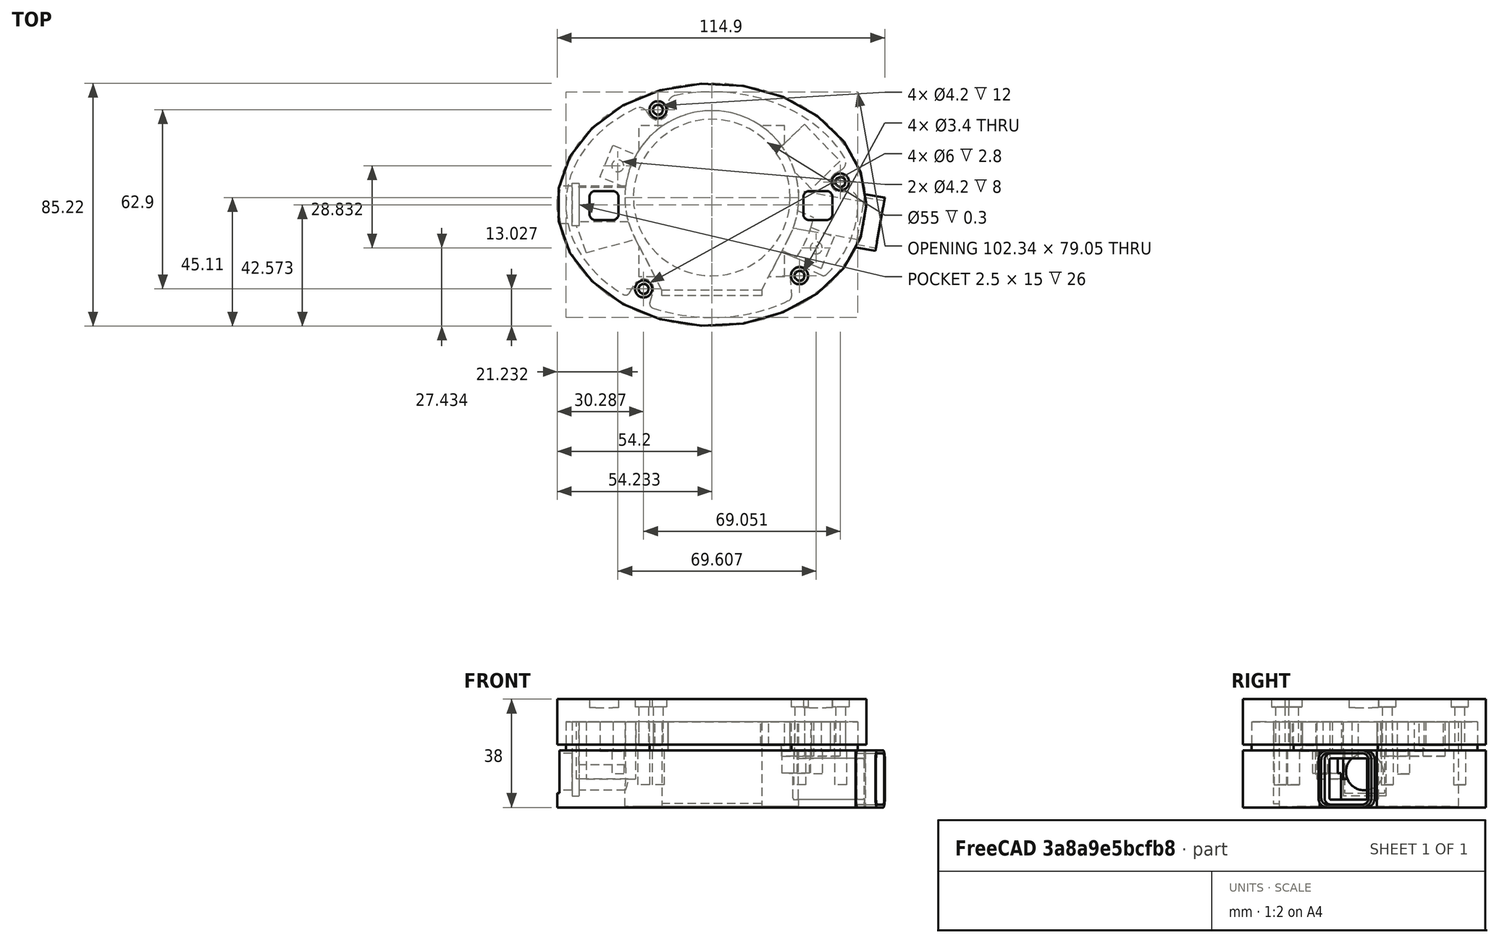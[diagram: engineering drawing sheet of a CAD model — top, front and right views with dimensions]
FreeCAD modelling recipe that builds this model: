
FCSTD DOCUMENT  (FreeCAD 0.21R32637 (Git))
Label: RGB-Case-Ellipse-SmallModel
License: All rights reserved
LicenseURL: http://en.wikipedia.org/wiki/All_rights_reserved
objects: Sketcher::SketchObject×25, PartDesign::Pocket×16, PartDesign::Line×8, PartDesign::Pad×5, PartDesign::Hole×5, PartDesign::Plane×2, PartDesign::SubShapeBinder×2, PartDesign::Body×2, PartDesign::SubtractiveCylinder×1, PartDesign::SubtractiveBox×1, PartDesign::ShapeBinder×1, PartDesign::FeatureBase×1
note: 97 computed .brp shape members not serialized (recipe doc carries the construction recipe); baked Part::Feature solids carry a one-line shape summary decoded from their .brp

FEATURE [Sketcher::SketchObject] Sketch
  FullyConstrained = true
  MapMode = 5
  Support = -> [XY_Plane001]
  sketch-geometry (9):
    g0: Ellipse CenterX=0 CenterY=0 CenterZ=0 NormalX=0 NormalY=0 NormalZ=1 MajorRadius=54.2041 MinorRadius=42.6127 AngleXU=-3.14159
    g1: LineSegment StartX=-54.2041 StartY=0 StartZ=0 EndX=54.2041 EndY=0 EndZ=0
    g2: LineSegment StartX=-1.358e-13 StartY=-42.6127 StartZ=0 EndX=1.358e-13 EndY=42.6127 EndZ=0
    g3: GeomPoint X=-33.5 Y=-1.727e-13 Z=0
    g4: GeomPoint X=33.5 Y=1.727e-13 Z=0
    g5: LineSegment StartX=-33.5 StartY=33.5 StartZ=0 EndX=33.5 EndY=33.5 EndZ=0
    g6: LineSegment StartX=33.5 StartY=33.5 StartZ=0 EndX=33.5 EndY=-33.5 EndZ=0
    g7: LineSegment StartX=33.5 StartY=-33.5 StartZ=0 EndX=-33.5 EndY=-33.5 EndZ=0
    g8: LineSegment StartX=-33.5 StartY=-33.5 StartZ=0 EndX=-33.5 EndY=33.5 EndZ=0
  constraints (17):
    c: InternalAlignment(g1-g4 -> g0) x4
    c: Coincident(g0,g-1)
    c: Horizontal(g1)
    c: Coincident(g5,g6)
    c: Coincident(g6,g7)
    c: Coincident(g7,g8)
    c: Coincident(g8,g5)
    c: Horizontal(g5)
    c: Horizontal(g7)
    c: Vertical(g6)
    c: Vertical(g8)
    c: PointOnObject(g5,g0)
    c: Symmetric(g5,g6,g0)
    c: DistanceY(g6,g6) = 67
    c: Equal(g6,g7)
    c: PointOnObject(g4,g6)
    c: DistanceX(g1,g3) = 20.7041
FEATURE [PartDesign::Pad] Pad  label="Aussenform"
  Direction = (0,0,1)
  Length = 30
  Length2 = 10
  Profile = -> Sketch
  ReferenceAxis = -> Sketch [N_Axis]
  Refine = true
  Type = 0
FEATURE [Sketcher::SketchObject] Sketch001
  ExternalGeometry = -> [Pad]
  FullyConstrained = true
  MapMode = 5
  Placement = pos=(0,0,30) rot=(0,0,1;0rad)
  Support = -> [Pad]
  expr: Constraints[11] = 65 / 2
  sketch-geometry (6):
    g0: LineSegment StartX=17.5 StartY=-30 StartZ=0 EndX=-17.5 EndY=-30 EndZ=0
    g1: ArcOfCircle CenterX=0 CenterY=2.5 CenterZ=0 NormalX=0 NormalY=0 NormalZ=1 AngleXU=0 Radius=30.5 StartAngle=5.80464 EndAngle=9.90332
    g2: LineSegment StartX=-17.5 StartY=-30 StartZ=0 EndX=-27.0738 EndY=-11.5449 EndZ=0
    g3: LineSegment StartX=17.5 StartY=-30 StartZ=0 EndX=27.0738 EndY=-11.5449 EndZ=0
    g4: GeomPoint X=0 Y=-30 Z=0
    g5: Circle CenterX=0 CenterY=2.5 CenterZ=0 NormalX=0 NormalY=0 NormalZ=1 AngleXU=0 Radius=30.5
  constraints (14):
    c: Horizontal(g0)
    c: DistanceX(g0,g0) = 35
    c: Diameter(g1) = 61
    c: DistanceY(g-1,g1) = 2.5
    c: PointOnObject(g1,g-2)
    c: Coincident(g2,g0)
    c: Coincident(g3,g0)
    c: Tangent(g1,g3) = -1.5708
    c: Tangent(g1,g2) = 1.5708
    c: PointOnObject(g4,g-2)
    c: Symmetric(g0,g0,g4)
    c: DistanceY(g4,g1) = 32.5
    c: Coincident(g5,g1)
    c: Equal(g5,g1)
FEATURE [PartDesign::Pocket] Pocket  label="Ausschnitt T-RGB"
  BaseFeature = -> Pad
  Direction = (0,0,-1)
  Length = 29.7
  Length2 = 5
  Profile = -> Sketch001
  ReferenceAxis = -> Sketch001 [N_Axis]
  Refine = true
  Type = 0
  expr: Length = <<Aussenform>>.Length - 0.3 mm
FEATURE [PartDesign::SubtractiveCylinder] Cylinder  label="Fenster Display"
  Angle = 360
  AttacherType = Attacher::AttachEngine3D
  BaseFeature = -> Pocket
  FirstAngle = 0
  Height = 2
  MapMode = 11
  Placement = pos=(3.6e-15,2.5,0.3) rot=(-0.519381,0.854543,0;3.14159rad)
  Radius = 27.5
  Refine = true
  SecondAngle = 0
  Support = -> [Pocket]
FEATURE [PartDesign::Plane] DatumPlane  label="DatumPlane - Height T-RGB"
  AttachmentOffset = pos=(0,0,19.5) rot=(0,0,1;0rad)
  Length = 134.685
  MapMode = 45
  Placement = pos=(-2.63e-14,-4.82293,19.8) rot=(0,0,1;0rad)
  ResizeMode = 0
  Support = -> [Cylinder]
  Width = 104.953
FEATURE [PartDesign::SubtractiveBox] Box  label="Box - Akku"
  AttacherType = Attacher::AttachEngine3D
  AttachmentOffset = pos=(-25.5,-20.5,2) rot=(0,0,1;0rad)
  BaseFeature = -> Cylinder
  Height = 16
  Length = 51
  MapMode = 5
  Placement = pos=(-25.5,-25.3229,21.8) rot=(0,0,1;0rad)
  Refine = true
  Support = -> [DatumPlane]
  Width = 53
  expr: .AttachmentOffset.Base.x = -Length / 2
  expr: .AttachmentOffset.Base.y = -(Width / 2) + 6 mm
FEATURE [PartDesign::Plane] DatumPlane001  label="DatumPlane - Height Battery"
  AttachmentOffset = pos=(0,0,7.5) rot=(0,0,1;0rad)
  Length = 134.685
  MapMode = 5
  Placement = pos=(-25.5,-25.3229,29.3) rot=(0,0,1;0rad)
  ResizeMode = 0
  Support = -> [Box]
  Width = 104.953
FEATURE [Sketcher::SketchObject] Sketch002
  ExternalGeometry = -> [Pad]
  FullyConstrained = true
  MapMode = 5
  Placement = pos=(0,0,30) rot=(0,0,1;0rad)
  Support = -> [Pad]
  sketch-geometry (12):
    g0: Ellipse CenterX=0 CenterY=0 CenterZ=0 NormalX=0 NormalY=0 NormalZ=1 MajorRadius=51.2041 MinorRadius=39.6127 AngleXU=0
    g1: LineSegment StartX=51.2041 StartY=0 StartZ=0 EndX=-51.2041 EndY=0 EndZ=0
    g2: LineSegment StartX=0 StartY=39.6127 StartZ=0 EndX=0 EndY=-39.6127 EndZ=0
    g3: GeomPoint X=32.4454 Y=0 Z=0
    g4: GeomPoint X=-32.4454 Y=0 Z=0
    g5: GeomPoint X=0 Y=42.6127 Z=0
    g6: GeomPoint X=54.2041 Y=0 Z=0
    g7: Ellipse CenterX=0 CenterY=0 CenterZ=0 NormalX=0 NormalY=0 NormalZ=1 MajorRadius=54.2041 MinorRadius=42.6127 AngleXU=-3.14159
    g8: LineSegment StartX=-54.2041 StartY=0 StartZ=0 EndX=54.2041 EndY=0 EndZ=0
    g9: LineSegment StartX=0 StartY=-42.6127 StartZ=0 EndX=0 EndY=42.6127 EndZ=0
    g10: GeomPoint X=-33.5 Y=0 Z=0
    g11: GeomPoint X=33.5 Y=0 Z=0
  constraints (12):
    c: InternalAlignment(g1-g4 -> g0) x4
    c: Coincident(g0,g-3)
    c: PointOnObject(g1,g-1)
    c: PointOnObject(g5,g-3)
    c: PointOnObject(g6,g-3)
    c: PointOnObject(g6,g-1)
    c: DistanceY(g2,g5) = 3
    c: DistanceX(g1,g6) = 3
    c: InternalAlignment(g8-g11 -> g7) x4
    c: Coincident(g7,g0)
    c: Coincident(g8,g6)
    c: Coincident(g9,g5)
FEATURE [PartDesign::Pocket] Pocket001  label="Pocket - Counterpart"
  BaseFeature = -> Box
  Direction = (0,0,-1)
  Length = 10
  Length2 = 5
  Placement = pos=(-25.5,-25.3229,21.8) rot=(0,0,1;0rad)
  Profile = -> Sketch002
  ReferenceAxis = -> Sketch002 [N_Axis]
  Refine = true
  Type = 0
  expr: Length = <<Aussenform>>.Length - 20 mm
FEATURE [Sketcher::SketchObject] Sketch003  label="Sketch SD"
  ExternalGeometry = -> [Pocket]
  FullyConstrained = true
  MapMode = 5
  Placement = pos=(0,0,30) rot=(0,0,1;0rad)
  Support = -> [Pocket]
  sketch-geometry (8):
    g0: LineSegment StartX=29.8059 StartY=-18.2995 StartZ=0 EndX=-2.93048 EndY=-4.40379 EndZ=0
    g1: LineSegment StartX=-2.93048 StartY=-4.40379 StartZ=0 EndX=2.93048 EndY=9.40379 EndZ=0
    g2: LineSegment StartX=2.93048 StartY=9.40379 StartZ=0 EndX=35.6668 EndY=-4.49198 EndZ=0
    g3: LineSegment StartX=32.7364 StartY=-11.3958 StartZ=0 EndX=0 EndY=2.5 EndZ=0
    g4: GeomPoint X=35.6668 Y=-4.49198 Z=0
    g5: GeomPoint X=30.1438 Y=-2.14759 Z=0
    g6: LineSegment StartX=35.6668 StartY=-4.49198 StartZ=0 EndX=29.8059 EndY=-18.2995 EndZ=0
    g7: ArcOfCircle CenterX=0 CenterY=2.5 CenterZ=0 NormalX=0 NormalY=0 NormalZ=1 AngleXU=0 Radius=36.3457 StartAngle=5.67391 EndAngle=6.0896
  constraints (18):
    c: Coincident(g0,g1)
    c: Coincident(g1,g2)
    c: Parallel(g0,g2)
    c: Perpendicular(g1,g2)
    c: Coincident(g4,g2)
    c: Coincident(g3,g-3)
    c: Angle(g-1,g3) = 2.74017
    c: PointOnObject(g5,g-3)
    c: PointOnObject(g5,g2)
    c: Distance(g5,g2) = 6
    c: Coincident(g6,g2)
    c: Coincident(g0,g6)
    c: Symmetric(g0,g1,g3)
    c: Distance(g1) = 15
    c: Coincident(g7,g3)
    c: Coincident(g7,g2)
    c: Coincident(g7,g0)
    c: Symmetric(g0,g2,g3)
FEATURE [PartDesign::Pocket] Pocket002  label="Pocket - SD"
  BaseFeature = -> Pocket001
  Direction = (0,0,-1)
  Length = 18
  Length2 = 20
  Placement = pos=(-25.5,-25.3229,21.8) rot=(0,0,1;0rad)
  Profile = -> Sketch003
  ReferenceAxis = -> Sketch003 [N_Axis]
  Refine = true
  Type = 0
  expr: Length = <<Aussenform>>.Length - 12 mm
FEATURE [Sketcher::SketchObject] Sketch004  label="Sketch USB-C"
  ExternalGeometry = -> [Pocket,Pad]
  FullyConstrained = true
  MapMode = 5
  Placement = pos=(0,0,30) rot=(0,0,1;0rad)
  Support = -> [Pocket]
  sketch-geometry (18):
    g0: LineSegment StartX=-29.2703 StartY=2.16279 StartZ=0 EndX=-49.0332 EndY=-3.13265 EndZ=0
    g1: LineSegment StartX=-47.7751 StartY=-2.79554 StartZ=0 EndX=-44.0222 EndY=-16.8015 EndZ=0
    g2: LineSegment StartX=-44.0222 StartY=-16.8015 StartZ=0 EndX=-25.5175 EndY=-11.8431 EndZ=0
    g3: LineSegment StartX=-25.5175 StartY=-11.8431 StartZ=0 EndX=-30.2985 EndY=6 EndZ=0
    g4: LineSegment StartX=-46.5277 StartY=-9.96706 StartZ=0 EndX=0 EndY=2.5 EndZ=0
    g5: ArcOfEllipse CenterX=0 CenterY=0 CenterZ=0 NormalX=0 NormalY=0 NormalZ=1 MajorRadius=49.2041 MinorRadius=37.6127 AngleXU=3.14159 StartAngle=0.0833837 EndAngle=0.46307
    g6: LineSegment StartX=-49.2041 StartY=0 StartZ=0 EndX=49.2041 EndY=0 EndZ=0
    g7: LineSegment StartX=0 StartY=-37.6127 StartZ=0 EndX=0 EndY=37.6127 EndZ=0
    g8: GeomPoint X=-31.7228 Y=0 Z=0
    g9: GeomPoint X=31.7228 Y=0 Z=0
    g10: GeomPoint X=0 Y=42.6127 Z=0
    g11: LineSegment StartX=0 StartY=37.6127 StartZ=0 EndX=0 EndY=42.6127 EndZ=0
    g12: LineSegment StartX=-49.2041 StartY=0 StartZ=0 EndX=-54.2041 EndY=0 EndZ=0
    g13: LineSegment StartX=-44.0222 StartY=-16.8015 StartZ=0 EndX=-49.0332 EndY=-3.13265 EndZ=0
    g14: LineSegment StartX=-30.2985 StartY=6 StartZ=0 EndX=-49.0332 EndY=6 EndZ=0
    g15: LineSegment StartX=-49.0332 StartY=-3.13265 StartZ=0 EndX=-49.0332 EndY=6 EndZ=0
    g16: GeomPoint X=-27.3939 Y=-4.84017 Z=0
    g17: GeomPoint X=-27.3939 Y=-4.84017 Z=0
  constraints (38):
    c: Coincident(g1,g2)
    c: Coincident(g2,g3)
    c: Parallel(g3,g1)
    c: Perpendicular(g3,g2)
    c: Perpendicular(g4,g1)
    c: Symmetric(g1,g0,g4)
    c: Angle(g-2,g4) = 1.8326
    c: Parallel(g0,g2)
    c: InternalAlignment(g6-g9 -> g5) x4
    c: Coincident(g5,g-4)
    c: PointOnObject(g6,g-1)
    c: Coincident(g5,g1)
    c: Coincident(g5,g0)
    c: PointOnObject(g10,g-4)
    c: PointOnObject(g10,g-2)
    c: Coincident(g4,g-3)
    c: PointOnObject(g1,g0)
    c: Coincident(g11,g7)
    c: Coincident(g11,g10)
    c: Coincident(g12,g6)
    c: PointOnObject(g12,g-4)
    c: PointOnObject(g12,g-1)
    c: DistanceX(g12,g12) = 5
    c: Equal(g12,g11)
    c: Coincident(g13,g2)
    c: Coincident(g13,g0)
    c: Distance(g13) = 14.5584
    c: Horizontal(g14)
    c: Coincident(g15,g13)
    c: Vertical(g15)
    c: Coincident(g14,g15)
    c: PointOnObject(g16,g3)
    c: Coincident(g17,g16)
    c: Coincident(g3,g14)
    c: Symmetric(g0,g2,g16)
    c: Distance(g0,g2) = 14.5
    c: PointOnObject(g3,g-3)
    c: DistanceY(g6,g14) = 6
FEATURE [PartDesign::Pocket] Pocket003  label="Pocket - USB-C"
  BaseFeature = -> Pocket002
  Direction = (0,0,-1)
  Length = 20
  Length2 = 20
  Placement = pos=(-25.5,-25.3229,21.8) rot=(0,0,1;0rad)
  Profile = -> Sketch004
  ReferenceAxis = -> Sketch004 [N_Axis]
  Refine = true
  Type = 0
FEATURE [Sketcher::SketchObject] Sketch005  label="Sketch - Halter T-RGB"
  FullyConstrained = true
  MapMode = 5
  Placement = pos=(0,0,30) rot=(0,0,1;0rad)
  Support = -> [Pocket]
  sketch-geometry (6):
    g0: LineSegment StartX=-34.6591 StartY=20.8506 StartZ=0 EndX=42.9468 EndY=-11.2948 EndZ=0
    g1: LineSegment StartX=42.9468 StartY=-11.2948 StartZ=0 EndX=38.3546 EndY=-22.3813 EndZ=0
    g2: LineSegment StartX=38.3546 StartY=-22.3813 StartZ=0 EndX=-39.2513 EndY=9.76406 EndZ=0
    g3: LineSegment StartX=-39.2513 StartY=9.76406 StartZ=0 EndX=-34.6591 EndY=20.8506 EndZ=0
    g4: LineSegment StartX=-36.9552 StartY=15.3073 StartZ=0 EndX=40.6507 EndY=-16.8381 EndZ=0
    g5: GeomPoint X=1.84776 Y=-0.765367 Z=0
  constraints (16):
    c: Coincident(g0,g1)
    c: Coincident(g1,g2)
    c: Coincident(g2,g3)
    c: Coincident(g3,g0)
    c: Parallel(g2,g0)
    c: Parallel(g3,g1)
    c: Perpendicular(g3,g0)
    c: PointOnObject(g4,g1)
    c: Symmetric(g0,g2,g4)
    c: Perpendicular(g3,g4)
    c: Distance(g3) = 12
    c: Distance(g2) = 84
    c: Symmetric(g4,g4,g5)
    c: PointOnObject(g-1,g4)
    c: Distance(g-1,g5) = 2
    c: Angle(g4,g-1) = 0.392699
FEATURE [PartDesign::Pocket] Pocket004  label="Pocket - Halter T-RGB"
  BaseFeature = -> Pocket003
  Direction = (0,0,-1)
  Length = 0
  Length2 = 5
  Offset = 2
  Placement = pos=(-25.5,-25.3229,21.8) rot=(0,0,1;0rad)
  Profile = -> Sketch005
  ReferenceAxis = -> Sketch005 [N_Axis]
  Refine = true
  Type = 3
  UpToFace = -> Pocket003 [Face27]
FEATURE [PartDesign::SubShapeBinder] Binder004  label="Binder - Klickfix Bodenplatte001"
  BindCopyOnChange = 0
  BindMode = 2
  ClaimChildren = false
  Fuse = false
  MakeFace = true
  OffsetFill = false
  OffsetIntersection = false
  OffsetJoinType = 0
  OffsetOpenResult = false
  PartialLoad = false
  Placement = pos=(-65.3,-42.8,44) rot=(0,0,1;0rad)
  Refine = true
  Relative = true
  _Version = 2
FEATURE [Sketcher::SketchObject] Sketch027
  ExternalGeometry = -> [Pocket004,Sketch003]
  FullyConstrained = true
  MapMode = 5
  Placement = pos=(-25.5,-25.3229,21.8) rot=(0,0,1;0rad)
  Support = -> [Pocket004]
  sketch-geometry (7):
    g0: LineSegment StartX=66.1507 StartY=8.48486 StartZ=0 EndX=-11.4552 EndY=40.6303 EndZ=0
    g1: Circle CenterX=62.139 CenterY=10.1466 CenterZ=0 NormalX=0 NormalY=0 NormalZ=1 AngleXU=0 Radius=2.5
    g2: Circle CenterX=-7.46824 CenterY=38.9788 CenterZ=0 NormalX=0 NormalY=0 NormalZ=1 AngleXU=0 Radius=2.5
    g3: GeomPoint X=-3.4813 Y=37.3274 Z=0
    g4: GeomPoint X=58.1273 Y=11.8083 Z=0
    g5: GeomPoint X=64.4487 Y=9.18985 Z=0
    g6: GeomPoint X=-5.15854 Y=38.0221 Z=0
  constraints (16):
    c: PointOnObject(g1,g0)
    c: PointOnObject(g2,g0)
    c: Equal(g2,g1)
    c: Diameter(g2) = 5
    c: Symmetric(g3,g0,g2)
    c: Symmetric(g4,g0,g1)
    c: PointOnObject(g5,g1)
    c: PointOnObject(g5,g0)
    c: Distance(g5,g0) = 1.84222
    c: PointOnObject(g6,g2)
    c: PointOnObject(g6,g0)
    c: Distance(g6,g3) = 1.81544
    c: Symmetric(g-3,g-3,g0)
    c: PointOnObject(g3,g-4)
    c: PointOnObject(g4,g-5)
    c: Symmetric(g-6,g-6,g0)
FEATURE [PartDesign::Hole] Hole
  BaseFeature = -> Pocket004
  CustomThreadClearance = 0
  Depth = 10
  DepthType = 0
  Diameter = 4.2
  DrillForDepth = false
  DrillPoint = 0
  DrillPointAngle = 118
  HoleCutCountersinkAngle = 90
  HoleCutCustomValues = false
  HoleCutDepth = 0
  HoleCutDiameter = 6.1
  HoleCutType = 0
  ModelThread = false
  Placement = pos=(-25.5,-25.3229,21.8) rot=(0,0,1;0rad)
  Profile = -> Sketch027
  Refine = true
  Tapered = true
  TaperedAngle = 90
  ThreadClass = 0
  ThreadDepth = 10
  ThreadDepthType = 0
  ThreadDirection = 0
  ThreadFit = 0
  ThreadSize = 13
  ThreadType = 1
  Threaded = true
  UseCustomThreadClearance = false
FEATURE [Sketcher::SketchObject] Sketch028  label="Sketch - Schalter"
  ExternalGeometry = -> [Hole]
  FullyConstrained = true
  MapMode = 5
  Placement = pos=(-25.5,-25.3229,20) rot=(0,0,1;0rad)
  Support = -> [Hole]
  sketch-geometry (4):
    g0: LineSegment StartX=-27.9678 StartY=18.3229 StartZ=0 EndX=-27.9678 EndY=32.3229 EndZ=0
    g1: LineSegment StartX=-27.9678 StartY=32.3229 StartZ=0 EndX=-29.9678 EndY=32.3229 EndZ=0
    g2: LineSegment StartX=-29.9678 StartY=32.3229 StartZ=0 EndX=-29.9678 EndY=18.3229 EndZ=0
    g3: LineSegment StartX=-29.9678 StartY=18.3229 StartZ=0 EndX=-27.9678 EndY=18.3229 EndZ=0
  constraints (12):
    c: PointOnObject(g0,g-3)
    c: PointOnObject(g0,g-3)
    c: Coincident(g1,g0)
    c: Coincident(g3,g0)
    c: Coincident(g2,g3)
    c: Coincident(g2,g1)
    c: Parallel(g2,g0)
    c: Perpendicular(g2,g1)
    c: Parallel(g3,g1)
    c: Distance(g0) = 14
    c: Distance(g3) = 2
    c: Vertical(g2)
FEATURE [PartDesign::Pocket] Pocket012  label="Pocket - Schalter"
  BaseFeature = -> Hole
  Direction = (-5e-16,-4e-16,-1)
  Length = 15
  Length2 = 5
  Placement = pos=(-25.5,-25.3229,21.8) rot=(0,0,1;0rad)
  Profile = -> Sketch028
  ReferenceAxis = -> Sketch028 [N_Axis]
  Refine = true
  Type = 0
FEATURE [Sketcher::SketchObject] Sketch029  label="Sketch - Bohrung Schalter"
  ExternalGeometry = -> [Pocket012]
  FullyConstrained = true
  MapMode = 5
  Placement = pos=(-53.4678,-25.3229,21.8) rot=(0.57735,-0.57735,-0.57735;2.0944rad)
  Support = -> [Pocket012]
  sketch-geometry (1):
    g0: Circle CenterX=-25.3229 CenterY=-9.3 CenterZ=0 NormalX=0 NormalY=0 NormalZ=1 AngleXU=0 Radius=6.5
  constraints (2):
    c: Symmetric(g-3,g-4,g0)
    c: Diameter(g0) = 13
FEATURE [PartDesign::Pocket] Pocket013  label="Pocket - Schalterbohrung"
  BaseFeature = -> Pocket012
  Direction = (1,4.426e-13,-6e-16)
  Length = 25
  Length2 = 5
  Placement = pos=(-25.5,-25.3229,21.8) rot=(0,0,1;0rad)
  Profile = -> Sketch029
  ReferenceAxis = -> Sketch029 [N_Axis]
  Refine = true
  Type = 0
FEATURE [Sketcher::SketchObject] Sketch030
  ExternalGeometry = -> [Pocket012]
  FullyConstrained = true
  MapMode = 5
  Placement = pos=(-25.5,-25.3229,10) rot=(0,0,1;0rad)
  Support = -> [Pocket013]
  sketch-geometry (5):
    g0: LineSegment StartX=-21.0332 StartY=17.8229 StartZ=0 EndX=-23.5332 EndY=17.8229 EndZ=0
    g1: LineSegment StartX=-23.5332 StartY=17.8229 StartZ=0 EndX=-23.5332 EndY=32.8229 EndZ=0
    g2: LineSegment StartX=-23.5332 StartY=32.8229 StartZ=0 EndX=-21.0332 EndY=32.8229 EndZ=0
    g3: LineSegment StartX=-21.0332 StartY=32.8229 StartZ=0 EndX=-21.0332 EndY=17.8229 EndZ=0
    g4: LineSegment StartX=-27.9678 StartY=25.3229 StartZ=0 EndX=-23.5332 EndY=25.3229 EndZ=0
  constraints (14):
    c: Coincident(g0,g1)
    c: Coincident(g1,g2)
    c: Coincident(g2,g3)
    c: Coincident(g3,g0)
    c: Parallel(g1,g3)
    c: Parallel(g0,g2)
    c: Perpendicular(g2,g3)
    c: Distance(g0) = 2.5
    c: Distance(g1) = 15
    c: Parallel(g1,g-3)
    c: Perpendicular(g4,g-3)
    c: Symmetric(g-3,g-3,g4)
    c: Symmetric(g0,g1,g4)
    c: PointOnObject(g-4,g1)
FEATURE [PartDesign::Pocket] Pocket014
  BaseFeature = -> Pocket013
  Direction = (-5e-16,-4e-16,-1)
  Length = 6
  Length2 = 35
  Placement = pos=(-25.5,-25.3229,21.8) rot=(0,0,1;0rad)
  Profile = -> Sketch030
  ReferenceAxis = -> Sketch030 [N_Axis]
  Refine = true
  Type = 4
FEATURE [Sketcher::SketchObject] Sketch009  label="Sketch - Counterpart"
  ExternalGeometry = -> [Pocket014]
  FullyConstrained = true
  MapMode = 5
  Placement = pos=(-25.5,-25.3229,30) rot=(0,0,1;0rad)
  Support = -> [Pocket014]
  sketch-geometry (45):
    g0: ArcOfCircle CenterX=56.283 CenterY=0.353162 CenterZ=0 NormalX=0 NormalY=0 NormalZ=1 AngleXU=0 Radius=3.28957 StartAngle=1.15839 EndAngle=3.20502
    g1: LineSegment StartX=53 StartY=0.144644 StartZ=0 EndX=53.4437 EndY=-6.84159 EndZ=0
    g2: LineSegment StartX=52.5986 StartY=-8.28762 StartZ=0 EndX=65.7452 EndY=0.832069 EndZ=0
    g3: ArcOfCircle CenterX=64.6934 CenterY=1.90153 CenterZ=0 NormalX=0 NormalY=0 NormalZ=1 AngleXU=0 Radius=1.5 StartAngle=4.29998 EndAngle=5.48945
    g4: GeomPoint X=65.7452 Y=0.832069 Z=0
    g5: GeomPoint X=59.1719 Y=-3.72777 Z=0
    g6: LineSegment StartX=64.0922 StartY=0.527293 StartZ=0 EndX=57.6015 EndY=3.36693 EndZ=0
    g7: ArcOfCircle CenterX=51.9467 CenterY=-6.93667 CenterZ=0 NormalX=0 NormalY=0 NormalZ=1 AngleXU=0 Radius=1.5 StartAngle=5.16197 EndAngle=6.34662
    g8: GeomPoint X=52.5986 Y=-8.28762 Z=0
    g9: LineSegment StartX=56.283 StartY=0.353162 StartZ=0 EndX=59.1719 EndY=-3.72777 EndZ=0
    g10: GeomPoint X=58.7679 Y=-3.15715 Z=0
    g11: ArcOfCircle CenterX=48.724 CenterY=11.3335 CenterZ=0 NormalX=0 NormalY=0 NormalZ=1 AngleXU=0 Radius=20 StartAngle=4.90735 EndAngle=5.73039
    g12: LineSegment StartX=10.2586 StartY=58.7802 StartZ=0 EndX=10.1885 EndY=60.6002 EndZ=0
    g13: ArcOfCircle CenterX=13.1862 CenterY=60.7157 CenterZ=0 NormalX=0 NormalY=0 NormalZ=1 AngleXU=0 Radius=3 StartAngle=1.76964 EndAngle=3.18009
    g14: ArcOfCircle CenterX=0.10421 CenterY=56.4221 CenterZ=0 NormalX=0 NormalY=0 NormalZ=1 AngleXU=0 Radius=3 StartAngle=0.595096 EndAngle=2.01195
    g15: LineSegment StartX=2.58849 StartY=58.1039 StartZ=0 EndX=3.6069 EndY=56.5995 EndZ=0
    g16: ArcOfCircle CenterX=11.524 CenterY=43.6852 CenterZ=0 NormalX=0 NormalY=0 NormalZ=1 AngleXU=0 Radius=20 StartAngle=1.51729 EndAngle=2.25885
    g17: ArcOfCircle CenterX=70.6383 CenterY=33.282 CenterZ=0 NormalX=0 NormalY=0 NormalZ=1 AngleXU=0 Radius=3.5 StartAngle=2.1074 EndAngle=4.78254
    g18: LineSegment StartX=71.0662 StartY=37.6089 StartZ=0 EndX=68.849 EndY=36.2901 EndZ=0
    g19: LineSegment StartX=70.8836 StartY=29.7906 StartZ=0 EndX=73.4443 EndY=29.9706 EndZ=0
    g20: ArcOfCircle CenterX=69.5325 CenterY=40.1873 CenterZ=0 NormalX=0 NormalY=0 NormalZ=1 AngleXU=0 Radius=3 StartAngle=5.24899 EndAngle=6.81413
    g21: ArcOfCircle CenterX=73.6546 CenterY=26.9779 CenterZ=0 NormalX=0 NormalY=0 NormalZ=1 AngleXU=0 Radius=3 StartAngle=0.0598538 EndAngle=1.64094
    g22: ArcOfCircle CenterX=56.7283 CenterY=28.9348 CenterZ=0 NormalX=0 NormalY=0 NormalZ=1 AngleXU=0 Radius=20 StartAngle=6.1942 EndAngle=6.97583
    g23: LineSegment StartX=3.6069 StartY=56.5995 StartZ=0 EndX=10.2586 EndY=58.7802 EndZ=0
    g24: ArcOfCircle CenterX=6.62121 CenterY=58.6401 CenterZ=0 NormalX=0 NormalY=0 NormalZ=1 AngleXU=0 Radius=3.64005 StartAngle=3.73669 EndAngle=6.32168
    g25: GeomPoint X=65.7452 Y=0.832077 Z=0
    g26: LineSegment StartX=6.93274 StartY=57.6898 StartZ=0 EndX=5.29349 EndY=62.69 EndZ=0
    g27: LineSegment StartX=57.6015 StartY=3.36693 StartZ=0 EndX=58.3668 EndY=5.21469 EndZ=0
    g28: LineSegment StartX=53 StartY=0.144644 StartZ=0 EndX=51 EndY=0.144644 EndZ=0
    g29: LineSegment StartX=71.0662 StartY=37.6089 StartZ=0 EndX=73.4443 EndY=29.9706 EndZ=0
    g30: LineSegment StartX=72.1195 StartY=41.7063 StartZ=0 EndX=76.6492 EndY=27.1574 EndZ=0
    g31: LineSegment StartX=25.5 StartY=25.3229 StartZ=0 EndX=70.6383 EndY=33.282 EndZ=0
    g32: GeomPoint X=55.8661 Y=30.6773 Z=0
    g33: LineSegment StartX=-3.47511 StartY=-5.71275 StartZ=0 EndX=-1.36974 EndY=-2.38736 EndZ=0
    g34: LineSegment StartX=3.80061 StartY=-9.03898 StartZ=0 EndX=4.93806 EndY=-5.27109 EndZ=0
    g35: ArcOfCircle CenterX=5.23661 CenterY=-9.47248 CenterZ=0 NormalX=0 NormalY=0 NormalZ=1 AngleXU=0 Radius=1.5 StartAngle=2.84841 EndAngle=4.38203
    g36: ArcOfCircle CenterX=-4.74246 CenterY=-4.91037 CenterZ=0 NormalX=0 NormalY=0 NormalZ=1 AngleXU=0 Radius=1.5 StartAngle=4.18042 EndAngle=5.71877
    g37: ArcOfCircle CenterX=1.58741 CenterY=-4.2596 CenterZ=0 NormalX=0 NormalY=0 NormalZ=1 AngleXU=0 Radius=3.5 StartAngle=5.99001 EndAngle=8.86036
    g38: ArcOfCircle CenterX=7.60289 CenterY=8.90412 CenterZ=0 NormalX=0 NormalY=0 NormalZ=1 AngleXU=0 Radius=20 StartAngle=3.9978 EndAngle=4.56926
    g39: LineSegment StartX=-3.47511 StartY=-5.71275 StartZ=0 EndX=3.80061 EndY=-9.03898 EndZ=0
    g40: LineSegment StartX=4.69424 StartY=-2.64789 StartZ=0 EndX=6.46957 EndY=-1.72691 EndZ=0
    g41: LineSegment StartX=9.56745 StartY=53.8307 StartZ=0 EndX=8.5227 EndY=55.5361 EndZ=0
    g42: LineSegment StartX=6.62121 StartY=53 StartZ=0 EndX=6.62121 EndY=55 EndZ=0
    g43: LineSegment StartX=1.58741 StartY=-4.2596 StartZ=0 EndX=-0.485744 EndY=-8.80954 EndZ=0
    g44: GeomPoint X=-0.485744 Y=-8.80954 Z=0
  constraints (115):
    c: Tangent(g0,g1) = -1.5708
    c: Distance(g0,g0) = 5.61753
    c: Coincident(g4,g3)
    c: Tangent(g6,g3) = 1.5708
    c: Tangent(g1,g7) = 1.5708
    c: Coincident(g9,g0)
    c: Coincident(g9,g5)
    c: PointOnObject(g10,g9)
    c: Symmetric(g3,g1,g10)
    c: Tangent(g6,g0) = -1.5708
    c: Coincident(g8,g7)
    c: Symmetric(g2,g2,g5)
    c: Coincident(g2,g7)
    c: Coincident(g2,g3)
    c: Distance(g2) = 16
    c: Distance(g9) = 5
    c: Coincident(g11,g3)
    c: Coincident(g11,g7)
    c: Radius(g11) = 20
    c: Coincident(g23,g12) = -1.5708
    c: Distance(g23,g15) = 7
    c: Tangent(g13,g12) = 1.5708
    c: Radius(g13) = 3
    c: Coincident(g16,g14)
    c: Coincident(g16,g13)
    c: Tangent(g18,g17) = -1.5708
    c: Tangent(g17,g19) = -1.5708
    c: Diameter(g17) = 7
    c: Tangent(g20,g18) = 1.5708
    c: Tangent(g21,g19) = 1.5708
    c: Coincident(g22,g20)
    c: Coincident(g22,g21)
    c: Tangent(g20,g-3) = -1.5708
    c: Tangent(g21,g-3) = -1.5708
    c: Tangent(g13,g-3) = -1.5708
    c: Tangent(g15,g14) = 1.5708
    c: Tangent(g14,g-3) = -1.5708
    c: Tangent(g24,g15) = -1.5708
    c: Tangent(g24,g12) = -1.5708
    c: Equal(g14,g13)
    c: Coincident(g15,g23)
    c: Tangent(g7,g-3) = -1.5708
    c: PointOnObject(g25,g-3)
    c: PointOnObject(g25,g3)
    c: Tangent(g-3,g3,g25) = -1.5708
    c: PointOnObject(g3,g-3)
    c: Equal(g3,g7)
    c: Radius(g7) = 1.5
    c: Equal(g21,g20)
    c: Radius(g21) = 3
    c: Equal(g11,g22)
    c: Equal(g22,g16)
    c: PointOnObject(g26,g23)
    c: PointOnObject(g26,g16)
    c: PointOnObject(g24,g26)
    c: Distance(g24,g26) = 1
    c: Perpendicular(g16,g26)
    c: Perpendicular(g23,g26)
    c: Coincident(g27,g0)
    c: PointOnObject(g27,g-5)
    c: Coincident(g28,g0)
    c: PointOnObject(g28,g-4)
    c: Horizontal(g28)
    c: Perpendicular(g-5,g27)
    c: Equal(g28,g27)
    c: Distance(g27) = 2
    c: Coincident(g29,g18)
    c: Coincident(g29,g19)
    c: Coincident(g30,g20)
    c: Coincident(g30,g21)
    c: Parallel(g29,g30)
    c: Distance(g29) = 8
    c: Coincident(g31,g-3)
    c: Coincident(g31,g17)
    c: PointOnObject(g32,g-6)
    c: PointOnObject(g32,g31)
    c: Distance(g32,g17) = 15
    c: Tangent(g35,g34) = 1.5708
    c: Tangent(g33,g36) = -1.5708
    c: Tangent(g37,g33) = 1.5708
    c: Tangent(g37,g34) = -1.5708
    c: Tangent(g35,g-3) = -1.5708
    c: Tangent(g36,g-3) = -1.5708
    c: Coincident(g38,g35)
    c: Coincident(g38,g36)
    c: Equal(g36,g35)
    c: Radius(g35) = 1.5
    c: Diameter(g37) = 7
    c: Equal(g34,g33)
    c: Coincident(g39,g33)
    c: Coincident(g39,g34)
    c: Distance(g39) = 8
    c: PointOnObject(g40,g37)
    c: PointOnObject(g40,g-7)
    c: Perpendicular(g37,g40)
    c: Perpendicular(g-7,g40)
    c: Distance(g40) = 2
    c: Equal(g38,g16)
    c: Angle(g31) = 0.174533
    c: PointOnObject(g41,g-9)
    c: PointOnObject(g42,g-8)
    c: PointOnObject(g42,g24)
    c: Perpendicular(g24,g42)
    c: Perpendicular(g24,g41)
    c: Perpendicular(g-9,g41)
    c: PointOnObject(g41,g24)
    c: Perpendicular(g-8,g42)
    c: Distance(g41) = 2
    c: Equal(g42,g41)
    c: Coincident(g43,g37)
    c: PointOnObject(g43,g-3)
    c: PointOnObject(g44,g-3)
    c: PointOnObject(g44,g43)
    c: Perpendicular(g-3,g43,g44) = 4.71239
    c: Distance(g43) = 5
FEATURE [PartDesign::Line] DatumLine004  label="DatumLine - Bohrung Schalter"
  AttacherType = Attacher::AttachEngineLine
  Length = 20
  MapMode = 19
  Placement = pos=(-53.4678,-1.41096e-11,12.5) rot=(0.57735,-0.57735,-0.57735;2.0944rad)
  ResizeMode = 0
  Support = -> [Pocket013]
FEATURE [PartDesign::Pocket] Pocket015  label="Pocket - Counterpart001"
  BaseFeature = -> Pocket014
  Direction = (-1e-15,-7e-16,-1)
  Length = 10
  Length2 = 5
  Placement = pos=(-25.5,-25.3229,21.8) rot=(0,0,1;0rad)
  Profile = -> Sketch009
  ReferenceAxis = -> Sketch009 [N_Axis]
  Refine = true
  Type = 0
FEATURE [Sketcher::SketchObject] Sketch031  label="Sketch - Counterpart Holes"
  ExternalGeometry = -> [Sketch009]
  FullyConstrained = true
  MapMode = 5
  Placement = pos=(-25.5,-25.3229,20) rot=(0,0,1;0rad)
  Support = -> [Pocket015]
  sketch-geometry (4):
    g0: Circle CenterX=6.62121 CenterY=58.6401 CenterZ=0 NormalX=0 NormalY=0 NormalZ=1 AngleXU=0 Radius=2.5
    g1: Circle CenterX=70.6383 CenterY=33.282 CenterZ=0 NormalX=0 NormalY=0 NormalZ=1 AngleXU=0 Radius=2.5
    g2: Circle CenterX=56.283 CenterY=0.353162 CenterZ=0 NormalX=0 NormalY=0 NormalZ=1 AngleXU=0 Radius=2.5
    g3: Circle CenterX=1.58741 CenterY=-4.2596 CenterZ=0 NormalX=0 NormalY=0 NormalZ=1 AngleXU=0 Radius=2.5
  constraints (8):
    c: Equal(g3,g0)
    c: Equal(g0,g1)
    c: Equal(g1,g2)
    c: Diameter(g3) = 5
    c: Coincident(g3,g-6)
    c: Coincident(g-5,g2)
    c: Coincident(g-4,g1)
    c: Coincident(g-3,g0)
FEATURE [PartDesign::Hole] Hole007  label="Hole - Counterpart"
  BaseFeature = -> Pocket015
  CustomThreadClearance = 0
  Depth = 12
  DepthType = 0
  Diameter = 4.2
  DrillForDepth = false
  DrillPoint = 0
  DrillPointAngle = 118
  HoleCutCountersinkAngle = 90
  HoleCutCustomValues = false
  HoleCutDepth = 0
  HoleCutDiameter = 6.1
  HoleCutType = 0
  ModelThread = false
  Placement = pos=(-25.5,-25.3229,21.8) rot=(0,0,1;0rad)
  Profile = -> Sketch031
  Refine = true
  Tapered = false
  TaperedAngle = 90
  ThreadClass = 0
  ThreadDepth = 12
  ThreadDepthType = 0
  ThreadDirection = 0
  ThreadFit = 0
  ThreadSize = 13
  ThreadType = 1
  Threaded = true
  UseCustomThreadClearance = false
FEATURE [PartDesign::ShapeBinder] ShapeBinder  label="ShapeBinder - Sketch Ausparung Gegenpart"
  Placement = pos=(-25.5,-25.3229,30) rot=(0,0,1;0rad)
  Support = -> [Sketch009]
  TraceSupport = false
FEATURE [PartDesign::SubShapeBinder] Binder006  label="Binder - Deckel Unterseite"
  BindCopyOnChange = 0
  BindMode = 1
  ClaimChildren = false
  Fuse = false
  MakeFace = true
  OffsetFill = false
  OffsetIntersection = false
  OffsetJoinType = 0
  OffsetOpenResult = false
  PartialLoad = false
  Refine = true
  Relative = true
  Support = -> [Body[Pocket015.Face3]]
  _Version = 2
FEATURE [PartDesign::FeatureBase] BaseFeature  label="BaseFeature - Shapebinder Deckel"
  BaseFeature = -> Binder006
FEATURE [Sketcher::SketchObject] Sketch019
  ExternalGeometry = -> [BaseFeature]
  FullyConstrained = true
  MapMode = 5
  Placement = pos=(3e-15,1.8e-15,30) rot=(0,0,1;0rad)
  Support = -> [BaseFeature]
  sketch-geometry (12):
    g0: Ellipse CenterX=0 CenterY=0 CenterZ=0 NormalX=0 NormalY=0 NormalZ=1 MajorRadius=51.2041 MinorRadius=39.6127 AngleXU=0
    g1: LineSegment StartX=51.2041 StartY=0 StartZ=0 EndX=-51.2041 EndY=0 EndZ=0
    g2: LineSegment StartX=0 StartY=39.6127 StartZ=0 EndX=0 EndY=-39.6127 EndZ=0
    g3: GeomPoint X=32.4454 Y=0 Z=0
    g4: GeomPoint X=-32.4454 Y=0 Z=0
    g5: GeomPoint X=0 Y=42.6127 Z=0
    g6: GeomPoint X=54.2041 Y=0 Z=0
    g7: Ellipse CenterX=0 CenterY=0 CenterZ=0 NormalX=0 NormalY=0 NormalZ=1 MajorRadius=54.2041 MinorRadius=42.6127 AngleXU=-3.14159
    g8: LineSegment StartX=-54.2041 StartY=0 StartZ=0 EndX=54.2041 EndY=0 EndZ=0
    g9: LineSegment StartX=0 StartY=-42.6127 StartZ=0 EndX=0 EndY=42.6127 EndZ=0
    g10: GeomPoint X=-33.5 Y=-4.1e-15 Z=0
    g11: GeomPoint X=33.5 Y=0 Z=0
  constraints (12):
    c: InternalAlignment(g1-g4 -> g0) x4
    c: PointOnObject(g1,g-1)
    c: PointOnObject(g6,g-1)
    c: DistanceY(g2,g5) = 3
    c: DistanceX(g1,g6) = 3
    c: InternalAlignment(g8-g11 -> g7) x4
    c: Coincident(g7,g0)
    c: Coincident(g8,g6)
    c: Coincident(g9,g5)
    c: Coincident(g0,g-1)
    c: PointOnObject(g2,g-3)
    c: PointOnObject(g1,g-3)
FEATURE [PartDesign::Pad] Pad005  label="Pad - Rand"
  BaseFeature = -> BaseFeature
  Direction = (1e-16,1e-16,1)
  Length = 8
  Length2 = 10
  Profile = -> Sketch019
  ReferenceAxis = -> Sketch019 [N_Axis]
  Refine = true
  Reversed = true
  Type = 0
FEATURE [Sketcher::SketchObject] Sketch020
  ExternalGeometry = -> [Sketch019]
  FullyConstrained = true
  MapMode = 5
  Placement = pos=(3e-15,1.8e-15,30) rot=(0,0,1;0rad)
  Support = -> [BaseFeature]
  sketch-geometry (5):
    g0: Ellipse CenterX=0 CenterY=0 CenterZ=0 NormalX=0 NormalY=0 NormalZ=1 MajorRadius=54.2041 MinorRadius=42.6127 AngleXU=0
    g1: LineSegment StartX=54.2041 StartY=0 StartZ=0 EndX=-54.2041 EndY=0 EndZ=0
    g2: LineSegment StartX=0 StartY=42.6127 StartZ=0 EndX=0 EndY=-42.6127 EndZ=0
    g3: GeomPoint X=33.5 Y=0 Z=0
    g4: GeomPoint X=-33.5 Y=0 Z=0
  constraints (5):
    c: InternalAlignment(g1-g4 -> g0) x4
    c: PointOnObject(g1,g-1)
    c: Coincident(g0,g-1)
    c: PointOnObject(g1,g-3)
    c: PointOnObject(g2,g-3)
FEATURE [PartDesign::Pad] Pad007  label="Pad - Boden"
  BaseFeature = -> Pad005
  Direction = (1e-16,1e-16,1)
  Length = 8
  Length2 = 10
  Profile = -> Sketch020
  ReferenceAxis = -> Sketch020 [N_Axis]
  Refine = true
  Type = 0
FEATURE [Sketcher::SketchObject] Sketch021
  ExternalGeometry = -> [Binder004]
  FullyConstrained = true
  MapMode = 5
  Placement = pos=(4.2e-15,1.8e-15,38) rot=(0,0,1;0rad)
  Support = -> [Pad007]
  sketch-geometry (24):
    g0: ArcOfCircle CenterX=-40.8 CenterY=2.7 CenterZ=0 NormalX=0 NormalY=0 NormalZ=1 AngleXU=0 Radius=2.1 StartAngle=1.5708 EndAngle=3.14159
    g1: LineSegment StartX=-40.8 StartY=4.8 StartZ=0 EndX=-34.8 EndY=4.8 EndZ=0
    g2: ArcOfCircle CenterX=-34.8 CenterY=2.7 CenterZ=0 NormalX=0 NormalY=0 NormalZ=1 AngleXU=0 Radius=2.1 StartAngle=1e-16 EndAngle=1.5708
    g3: LineSegment StartX=-32.7 StartY=2.7 StartZ=0 EndX=-32.7 EndY=-3.3 EndZ=0
    g4: ArcOfCircle CenterX=-34.8 CenterY=-3.3 CenterZ=0 NormalX=0 NormalY=0 NormalZ=1 AngleXU=0 Radius=2.1 StartAngle=4.71239 EndAngle=6.28319
    g5: LineSegment StartX=-34.8 StartY=-5.4 StartZ=0 EndX=-40.8 EndY=-5.4 EndZ=0
    g6: ArcOfCircle CenterX=-40.8 CenterY=-3.3 CenterZ=0 NormalX=0 NormalY=0 NormalZ=1 AngleXU=0 Radius=2.1 StartAngle=3.14159 EndAngle=4.71239
    g7: LineSegment StartX=-42.9 StartY=-3.3 StartZ=0 EndX=-42.9 EndY=2.7 EndZ=0
    g8: GeomPoint X=-42.9 Y=4.8 Z=0
    g9: GeomPoint X=-32.7 Y=-5.4 Z=0
    g10: ArcOfCircle CenterX=34.2 CenterY=2.7 CenterZ=0 NormalX=0 NormalY=0 NormalZ=1 AngleXU=0 Radius=2.1 StartAngle=1.5708 EndAngle=3.14159
    g11: LineSegment StartX=34.2 StartY=4.8 StartZ=0 EndX=40.2 EndY=4.8 EndZ=0
    g12: ArcOfCircle CenterX=40.2 CenterY=2.7 CenterZ=0 NormalX=0 NormalY=0 NormalZ=1 AngleXU=0 Radius=2.1 StartAngle=0 EndAngle=1.5708
    g13: LineSegment StartX=42.3 StartY=2.7 StartZ=0 EndX=42.3 EndY=-3.3 EndZ=0
    g14: ArcOfCircle CenterX=40.2 CenterY=-3.3 CenterZ=0 NormalX=0 NormalY=0 NormalZ=1 AngleXU=0 Radius=2.1 StartAngle=4.71239 EndAngle=6.28319
    g15: LineSegment StartX=40.2 StartY=-5.4 StartZ=0 EndX=34.2 EndY=-5.4 EndZ=0
    g16: ArcOfCircle CenterX=34.2 CenterY=-3.3 CenterZ=0 NormalX=0 NormalY=0 NormalZ=1 AngleXU=0 Radius=2.1 StartAngle=3.14159 EndAngle=4.71239
    g17: LineSegment StartX=32.1 StartY=-3.3 StartZ=0 EndX=32.1 EndY=2.7 EndZ=0
    g18: GeomPoint X=32.1 Y=4.8 Z=0
    g19: GeomPoint X=42.3 Y=-5.4 Z=0
    g20: LineSegment StartX=-40.8 StartY=4.7 StartZ=0 EndX=-40.8 EndY=4.8 EndZ=0
    g21: LineSegment StartX=-32.8 StartY=-3.3 StartZ=0 EndX=-32.7 EndY=-3.3 EndZ=0
    g22: LineSegment StartX=42.2 StartY=-3.3 StartZ=0 EndX=42.3 EndY=-3.3 EndZ=0
    g23: LineSegment StartX=34.2 StartY=4.7 StartZ=0 EndX=34.2 EndY=4.8 EndZ=0
  constraints (52):
    c: Tangent(g0,g1) = 1.5708
    c: Tangent(g1,g2) = 1.5708
    c: Tangent(g2,g3) = 1.5708
    c: Tangent(g3,g4) = 1.5708
    c: Tangent(g4,g5) = 1.5708
    c: Tangent(g5,g6) = 1.5708
    c: Tangent(g6,g7) = 1.5708
    c: Tangent(g7,g0) = 1.5708
    c: Horizontal(g1)
    c: Horizontal(g5)
    c: Vertical(g3)
    c: Vertical(g7)
    c: Equal(g2,g4)
    c: Equal(g4,g6)
    c: PointOnObject(g8,g1)
    c: PointOnObject(g8,g7)
    c: PointOnObject(g9,g3)
    c: PointOnObject(g9,g5)
    c: Tangent(g10,g11) = 1.5708
    c: Tangent(g11,g12) = 1.5708
    c: Tangent(g12,g13) = 1.5708
    c: Tangent(g13,g14) = 1.5708
    c: Tangent(g14,g15) = 1.5708
    c: Tangent(g15,g16) = 1.5708
    c: Tangent(g16,g17) = 1.5708
    c: Tangent(g17,g10) = 1.5708
    c: Horizontal(g11)
    c: Horizontal(g15)
    c: Vertical(g13)
    c: Vertical(g17)
    c: Equal(g10,g12)
    c: Equal(g12,g14)
    c: PointOnObject(g18,g11)
    c: PointOnObject(g18,g17)
    c: PointOnObject(g19,g13)
    c: PointOnObject(g19,g15)
    c: Coincident(g-4,g4)
    c: Coincident(g-3,g0)
    c: DistanceY(g-3,g0) = 0.1
    c: Coincident(g20,g-3)
    c: Coincident(g20,g0)
    c: Coincident(g21,g-4)
    c: Coincident(g21,g3)
    c: Equal(g21,g20)
    c: Coincident(g14,g-6)
    c: Coincident(g-5,g10)
    c: Coincident(g22,g-6)
    c: Coincident(g22,g13)
    c: Equal(g16,g14)
    c: Coincident(g23,g-5)
    c: Coincident(g23,g10)
    c: Equal(g23,g20)
FEATURE [PartDesign::Pocket] Pocket008  label="Pocket - KF Anbindung"
  BaseFeature = -> Pad007
  Direction = (-1e-16,0,-1)
  Length = 3
  Length2 = 5
  Profile = -> Sketch021
  ReferenceAxis = -> Sketch021 [N_Axis]
  Refine = true
  Type = 0
FEATURE [Sketcher::SketchObject] Sketch022  label="Sketch - Bohrungen KF Anbindung"
  ExternalGeometry = -> [Pocket008]
  FullyConstrained = true
  MapMode = 5
  Placement = pos=(3.3e-15,1.4e-15,30) rot=(1,0,0;3.14159rad)
  Support = -> [Pocket008]
  sketch-geometry (6):
    g0: GeomPoint X=-37.8 Y=0.3 Z=0
    g1: GeomPoint X=37.2 Y=0.3 Z=0
    g2: Circle CenterX=-37.8 CenterY=0.3 CenterZ=0 NormalX=0 NormalY=0 NormalZ=1 AngleXU=0 Radius=1.5
    g3: Circle CenterX=37.2 CenterY=0.3 CenterZ=0 NormalX=0 NormalY=0 NormalZ=1 AngleXU=0 Radius=1.5
    g4: GeomPoint X=-37.8 Y=0.3 Z=0
    g5: GeomPoint X=37.2 Y=0.3 Z=0
  constraints (8):
    c: Coincident(g2,g0)
    c: Coincident(g3,g1)
    c: Equal(g3,g2)
    c: Diameter(g2) = 3
    c: Symmetric(g-3,g-4,g4)
    c: Coincident(g2,g4)
    c: Symmetric(g-6,g-5,g5)
    c: Coincident(g5,g3)
FEATURE [Sketcher::SketchObject] Sketch024  label="Sketch - Zugang Strom"
  ExternalGeometry = -> [BaseFeature]
  FullyConstrained = true
  MapMode = 5
  Placement = pos=(3.3e-15,1.4e-15,30) rot=(1,0,0;3.14159rad)
  Support = -> [Pad007]
  sketch-geometry (4):
    g0: Circle CenterX=13.9553 CenterY=23.85 CenterZ=0 NormalX=0 NormalY=0 NormalZ=1 AngleXU=0 Radius=10
    g1: LineSegment StartX=17.7615 StartY=37.1531 StartZ=0 EndX=16.7061 EndY=33.4642 EndZ=0
    g2: GeomPoint X=17.7615 Y=37.1531 Z=0
    g3: Circle CenterX=13.9553 CenterY=23.85 CenterZ=0 NormalX=0 NormalY=0 NormalZ=1 AngleXU=0 Radius=6.15
  constraints (12):
    c: Diameter(g0) = 20
    c: PointOnObject(g1,g-3)
    c: PointOnObject(g2,g-3)
    c: PointOnObject(g2,g1)
    c: Perpendicular(g-3,g1,g2) = 1.5708
    c: Perpendicular(g0,g1)
    c: PointOnObject(g1,g0)
    c: Distance(g1) = 3.83694
    c: Coincident(g3,g0)
    c: Diameter(g3) = 12.3
    c: PointOnObject(g-5,g3)
    c: Tangent(g3,g-4)
FEATURE [PartDesign::Pad] Pad008  label="Pad - Ausparung Gegenpart"
  BaseFeature = -> Pocket008
  Direction = (1e-15,1e-15,1)
  Length = 8
  Length2 = 10
  Profile = -> ShapeBinder
  Refine = true
  Reversed = true
  Type = 0
FEATURE [Sketcher::SketchObject] Sketch032
  ExternalGeometry = -> [Pad008]
  FullyConstrained = true
  MapMode = 5
  Placement = pos=(4.2e-15,1.8e-15,38) rot=(0,0,1;0rad)
  Support = -> [Pad007]
  sketch-geometry (4):
    g0: Circle CenterX=-23.9126 CenterY=-29.5825 CenterZ=0 NormalX=0 NormalY=0 NormalZ=1 AngleXU=0 Radius=2.5
    g1: Circle CenterX=30.783 CenterY=-24.9698 CenterZ=0 NormalX=0 NormalY=0 NormalZ=1 AngleXU=0 Radius=2.5
    g2: Circle CenterX=45.1383 CenterY=7.95909 CenterZ=0 NormalX=0 NormalY=0 NormalZ=1 AngleXU=0 Radius=2.5
    g3: Circle CenterX=-18.8788 CenterY=33.3171 CenterZ=0 NormalX=0 NormalY=0 NormalZ=1 AngleXU=0 Radius=2.5
  constraints (8):
    c: Coincident(g0,g-3)
    c: Coincident(g1,g-5)
    c: Coincident(g-6,g2)
    c: Coincident(g3,g-4)
    c: Equal(g1,g2)
    c: Equal(g2,g3)
    c: Equal(g3,g0)
    c: Diameter(g0) = 5
FEATURE [PartDesign::Hole] Hole008  label="Hole - Bohrlöcher Gegenpart"
  BaseFeature = -> Pad008
  CustomThreadClearance = 0
  Depth = 25
  DepthType = 0
  Diameter = 3.4
  DrillForDepth = false
  DrillPoint = 0
  DrillPointAngle = 118
  HoleCutCountersinkAngle = 90
  HoleCutCustomValues = false
  HoleCutDepth = 2.8
  HoleCutDiameter = 6
  HoleCutType = 6
  ModelThread = false
  Profile = -> Sketch032
  Refine = true
  Tapered = false
  TaperedAngle = 90
  ThreadClass = 0
  ThreadDepth = 25
  ThreadDepthType = 0
  ThreadDirection = 0
  ThreadFit = 0
  ThreadSize = 9
  ThreadType = 1
  Threaded = false
  UseCustomThreadClearance = false
FEATURE [PartDesign::Hole] Hole004  label="Hole - Bohrungen KF Anbindung"
  BaseFeature = -> Hole008
  CustomThreadClearance = 0
  Depth = 25
  DepthType = 0
  Diameter = 4.5
  DrillForDepth = false
  DrillPoint = 1
  DrillPointAngle = 118
  HoleCutCountersinkAngle = 90
  HoleCutCustomValues = false
  HoleCutDepth = 3.2
  HoleCutDiameter = 8
  HoleCutType = 4
  ModelThread = false
  Profile = -> Sketch022
  Refine = true
  Tapered = false
  TaperedAngle = 90
  ThreadClass = 0
  ThreadDepth = 25
  ThreadDepthType = 0
  ThreadDirection = 0
  ThreadFit = 0
  ThreadSize = 11
  ThreadType = 1
  Threaded = false
  UseCustomThreadClearance = false
FEATURE [PartDesign::Hole] Hole006
  BaseFeature = -> Hole004
  CustomThreadClearance = 0
  Depth = 25
  DepthType = 0
  Diameter = 12.5
  DrillForDepth = false
  DrillPoint = 1
  DrillPointAngle = 118
  HoleCutCountersinkAngle = 90
  HoleCutCustomValues = false
  HoleCutDepth = 5.5
  HoleCutDiameter = 20
  HoleCutType = 1
  ModelThread = false
  Profile = -> Sketch024
  Refine = true
  Tapered = false
  TaperedAngle = 90
  ThreadClass = 0
  ThreadDepth = 25
  ThreadDepthType = 0
  ThreadDirection = 0
  ThreadFit = 0
  ThreadSize = 0
  ThreadType = 0
  Threaded = false
  UseCustomThreadClearance = false
FEATURE [Sketcher::SketchObject] MirroredSketch  label="Sketch - Kabelführung"
  ExternalGeometry = -> [Pad007,Hole006,BaseFeature]
  FullyConstrained = true
  MapMode = 5
  Placement = pos=(3.3e-15,1.4e-15,30) rot=(1,0,0;3.14159rad)
  Support = -> [Pad007]
  sketch-geometry (22):
    g0: LineSegment StartX=-7.87332 StartY=-2.39655 StartZ=0 EndX=-20.8733 EndY=-2.39655 EndZ=0
    g1: LineSegment StartX=-20.8733 StartY=-2.39655 StartZ=0 EndX=-20.8733 EndY=16.6035 EndZ=0
    g2: LineSegment StartX=-1.88704 StartY=-1.42887 StartZ=0 EndX=-7.87332 EndY=16.6035 EndZ=0
    g3: LineSegment StartX=-7.87332 StartY=16.6035 StartZ=0 EndX=-7.87332 EndY=-2.39655 EndZ=0
    g4: LineSegment StartX=1.25 StartY=34.9998 StartZ=0 EndX=14.8268 EndY=33.8119 EndZ=0
    g5: LineSegment StartX=10.4509 StartY=2.66701 StartZ=0 EndX=4.46458 EndY=20.6993 EndZ=0
    g6: ArcOfCircle CenterX=13.9553 CenterY=23.85 CenterZ=0 NormalX=0 NormalY=0 NormalZ=1 AngleXU=0 Radius=10 StartAngle=3.46212 EndAngle=7.76672
    g7: LineSegment StartX=1.25 StartY=34.9998 StartZ=0 EndX=1.25 EndY=39.6009 EndZ=0
    g8: LineSegment StartX=-1.25 StartY=34.9998 StartZ=0 EndX=-1.25 EndY=39.6009 EndZ=0
    g9: LineSegment StartX=1.25 StartY=39.6009 StartZ=0 EndX=-1.25 EndY=39.6009 EndZ=0
    g10: LineSegment StartX=-1.25 StartY=34.9998 StartZ=0 EndX=1.25 EndY=34.9998 EndZ=0
    g11: LineSegment StartX=-1.88704 StartY=-1.42887 StartZ=0 EndX=10.4509 EndY=2.66701 EndZ=0
    g12: LineSegment StartX=-1.25 StartY=34.9998 StartZ=0 EndX=-14.0568 EndY=30.3385 EndZ=0
    g13: ArcOfCircle CenterX=-10.5135 CenterY=20.6035 CenterZ=0 NormalX=0 NormalY=0 NormalZ=1 AngleXU=0 Radius=10.3598 StartAngle=1.91986 EndAngle=3.14159
    g14: LineSegment StartX=-20.8733 StartY=16.6035 StartZ=0 EndX=-20.8733 EndY=20.6035 EndZ=0
    g15: LineSegment StartX=-20.8733 StartY=20.6035 StartZ=0 EndX=-24.2565 EndY=20.3075 EndZ=0
    g16: LineSegment StartX=-20.8733 StartY=16.6035 StartZ=0 EndX=-24.5763 EndY=12.9005 EndZ=0
    g17: LineSegment StartX=-25.0156 StartY=11.8398 StartZ=0 EndX=-25.0156 EndY=3.83981 EndZ=0
    g18: LineSegment StartX=-25.0156 StartY=3.83981 StartZ=0 EndX=-32.0156 EndY=3.83981 EndZ=0
    g19: LineSegment StartX=-32.0156 StartY=3.83981 StartZ=0 EndX=-32.0156 EndY=11.8398 EndZ=0
    g20: ArcOfCircle CenterX=-23.5156 CenterY=11.8398 CenterZ=0 NormalX=0 NormalY=0 NormalZ=1 AngleXU=0 Radius=8.5 StartAngle=1.65806 EndAngle=3.14159
    g21: ArcOfCircle CenterX=-23.5156 CenterY=11.8398 CenterZ=0 NormalX=0 NormalY=0 NormalZ=1 AngleXU=0 Radius=1.5 StartAngle=2.35619 EndAngle=3.14159
  constraints (57):
    c: Coincident(g0,g3)
    c: Perpendicular(g0,g1)
    c: Coincident(g0,g1)
    c: Distance(g0) = 13
    c: Coincident(g2,g3)
    c: Equal(g2,g3)
    c: Parallel(g5,g2)
    c: Equal(g5,g2)
    c: Tangent(g6,g5) = 1.5708
    c: Tangent(g4,g6) = 1.5708
    c: Radius(g6) = 10
    c: Vertical(g7)
    c: Vertical(g8)
    c: Coincident(g9,g7)
    c: Coincident(g9,g8)
    c: Symmetric(g7,g8,g-2)
    c: PointOnObject(g7,g-3)
    c: Coincident(g7,g4)
    c: Coincident(g10,g4)
    c: Horizontal(g10)
    c: DistanceX(g8,g4) = 2.5
    c: Distance(g0,g1) = 19
    c: Coincident(g-4,g6)
    c: Parallel(g3,g1)
    c: Coincident(g11,g2)
    c: Coincident(g11,g5)
    c: Perpendicular(g2,g11)
    c: Equal(g0,g11)
    c: Coincident(g12,g8)
    c: Tangent(g12,g13) = -1.5708
    c: Coincident(g8,g10)
    c: Angle(g12) = -2.79253
    c: Angle(g4) = -0.0872665
    c: Equal(g12,g4)
    c: Equal(g1,g5)
    c: Vertical(g1)
    c: Coincident(g14,g1)
    c: Tangent(g14,g13) = 1.5708
    c: Vertical(g14)
    c: Coincident(g15,g13)
    c: Coincident(g16,g1)
    c: Vertical(g17)
    c: Coincident(g18,g17)
    c: Coincident(g18,g19)
    c: Horizontal(g18)
    c: Tangent(g15,g20) = -1.5708
    c: Tangent(g19,g20) = 1.5708
    c: Tangent(g17,g21) = -1.5708
    c: Tangent(g16,g21) = -1.5708
    c: DistanceY(g14,g14) = 4
    c: Coincident(g20,g21)
    c: Vertical(g19)
    c: Angle(g16,g1) = 0.785398
    c: DistanceX(g18,g18) = 7
    c: Radius(g21) = 1.5
    c: DistanceY(g17,g17) = 8
    c: Angle(g15) = -3.05433
FEATURE [PartDesign::Pocket] Pocket016  label="Pocket Kabelführung / Wago 221"
  BaseFeature = -> Hole006
  Direction = (1e-16,0,1)
  Length = 6
  Length2 = 5
  Profile = -> MirroredSketch
  ReferenceAxis = -> MirroredSketch [N_Axis]
  Refine = true
  Type = 0
FEATURE [Sketcher::SketchObject] Sketch026  label="Sketch - Wasserablauf"
  ExternalGeometry = -> [Pocket016]
  FullyConstrained = true
  MapMode = 5
  Placement = pos=(3.3e-15,1.4e-15,30) rot=(1,0,0;3.14159rad)
  Support = -> [Pad007]
  sketch-geometry (10):
    g0: ArcOfCircle CenterX=-1 CenterY=39.3509 CenterZ=0 NormalX=0 NormalY=0 NormalZ=1 AngleXU=0 Radius=0.25 StartAngle=1.5708 EndAngle=3.14159
    g1: LineSegment StartX=-1 StartY=39.6009 StartZ=0 EndX=1 EndY=39.6009 EndZ=0
    g2: ArcOfCircle CenterX=1 CenterY=39.3509 CenterZ=0 NormalX=0 NormalY=0 NormalZ=1 AngleXU=0 Radius=0.25 StartAngle=-4.4e-15 EndAngle=1.5708
    g3: LineSegment StartX=1.25 StartY=39.3509 StartZ=0 EndX=1.25 EndY=38.8509 EndZ=0
    g4: ArcOfCircle CenterX=1 CenterY=38.8509 CenterZ=0 NormalX=0 NormalY=0 NormalZ=1 AngleXU=0 Radius=0.25 StartAngle=4.71239 EndAngle=6.28319
    g5: LineSegment StartX=1 StartY=38.6009 StartZ=0 EndX=-1 EndY=38.6009 EndZ=0
    g6: ArcOfCircle CenterX=-1 CenterY=38.8509 CenterZ=0 NormalX=0 NormalY=0 NormalZ=1 AngleXU=0 Radius=0.25 StartAngle=3.14159 EndAngle=4.71239
    g7: LineSegment StartX=-1.25 StartY=38.8509 StartZ=0 EndX=-1.25 EndY=39.3509 EndZ=0
    g8: GeomPoint X=-1.25 Y=39.6009 Z=0
    g9: GeomPoint X=1.25 Y=38.6009 Z=0
  constraints (22):
    c: Tangent(g0,g1) = 1.5708
    c: Tangent(g1,g2) = 1.5708
    c: Tangent(g2,g3) = 1.5708
    c: Tangent(g3,g4) = 1.5708
    c: Tangent(g4,g5) = 1.5708
    c: Tangent(g5,g6) = 1.5708
    c: Tangent(g6,g7) = 1.5708
    c: Tangent(g7,g0) = 1.5708
    c: Horizontal(g1)
    c: Horizontal(g5)
    c: Vertical(g3)
    c: Vertical(g7)
    c: Equal(g2,g4)
    c: Equal(g4,g6)
    c: PointOnObject(g8,g1)
    c: PointOnObject(g8,g7)
    c: PointOnObject(g9,g3)
    c: PointOnObject(g9,g5)
    c: Symmetric(g2,g0,g-2)
    c: Radius(g6) = 0.25
    c: DistanceY(g4,g1) = 1
    c: Coincident(g8,g-3)
FEATURE [PartDesign::Pocket] Pocket010  label="Pocket - Wasserablauf"
  BaseFeature = -> Pocket016
  Direction = (1e-16,0,1)
  Length = 5
  Length2 = 5
  Profile = -> Sketch026
  ReferenceAxis = -> Sketch026 [N_Axis]
  Refine = true
  Type = 1
FEATURE [PartDesign::Line] DatumLine  label="DatumLine - KF l001"
  AttacherType = Attacher::AttachEngineLine
  Length = 20
  MapMode = 19
  Placement = pos=(37.2,-0.3,35) rot=(0,0,1;3.14159rad)
  ResizeMode = 0
  Support = -> [Pocket010]
FEATURE [PartDesign::Line] DatumLine005  label="DatumLine - KF r"
  AttacherType = Attacher::AttachEngineLine
  Length = 20
  MapMode = 19
  Placement = pos=(-37.8,-0.3,35) rot=(0,0,1;3.14159rad)
  ResizeMode = 0
  Support = -> [Pocket010]
FEATURE [PartDesign::Line] DatumLine006
  AttacherType = Attacher::AttachEngineLine
  Length = 20
  MapMode = 19
  Placement = pos=(-23.9126,-29.5825,38) rot=(0,0,1;0rad)
  ResizeMode = 0
  Support = -> [Pocket010]
FEATURE [PartDesign::Line] DatumLine007
  AttacherType = Attacher::AttachEngineLine
  Length = 20
  MapMode = 19
  Placement = pos=(-18.8788,33.3171,38) rot=(0,0,1;0rad)
  ResizeMode = 0
  Support = -> [Pocket010]
FEATURE [PartDesign::Line] DatumLine008
  AttacherType = Attacher::AttachEngineLine
  Length = 20
  MapMode = 19
  Placement = pos=(45.1383,7.95909,38) rot=(0,0,1;0rad)
  ResizeMode = 0
  Support = -> [Pocket010]
FEATURE [PartDesign::Line] DatumLine009
  AttacherType = Attacher::AttachEngineLine
  Length = 20
  MapMode = 19
  Placement = pos=(13.9553,-23.85,38) rot=(0,0,1;3.14159rad)
  ResizeMode = 0
  Support = -> [Pocket010]
FEATURE [PartDesign::Line] HoleAxis_4
  AttacherType = Attacher::AttachEngineLine
  Length = 17.6133
  MapMode = 19
  Placement = pos=(13.9553,-23.85,38) rot=(0,0,1;3.14159rad)
  ResizeMode = 1
  Support = -> [Hole006]
FEATURE [PartDesign::Body] Body002  label="Boden002"
  BaseFeature = -> Binder006
  Group = -> [BaseFeature,Sketch019,Pad005,Sketch020,Pad007,Binder004,Sketch021,Pocket008,Sketch022,ShapeBinder,Pad008,Sketch032,Hole008,DatumLine,DatumLine005,DatumLine006,DatumLine007,DatumLine008,DatumLine009,HoleAxis_4,Hole004,Sketch024,Hole006,Sketch026,MirroredSketch,Pocket016,Pocket010]
  Origin = -> Origin006
  Tip = -> Hole008
FEATURE [Sketcher::SketchObject] Sketch033
  ExternalGeometry = -> [Pad]
  FullyConstrained = true
  MapMode = 5
  Placement = pos=(0,0,30) rot=(0,0,1;0rad)
  Support = -> [Pad]
  sketch-geometry (4):
    g0: LineSegment StartX=53.9254 StartY=4.31557 StartZ=0 EndX=55.4364 EndY=4.04915 EndZ=0
    g1: LineSegment StartX=55.4364 StartY=4.04915 StartZ=0 EndX=51.9099 EndY=-15.9509 EndZ=0
    g2: LineSegment StartX=51.9099 StartY=-15.9509 StartZ=0 EndX=50.3989 EndY=-15.6844 EndZ=0
    g3: LineSegment StartX=50.3989 StartY=-15.6844 StartZ=0 EndX=53.9254 EndY=4.31557 EndZ=0
  constraints (12):
    c: Coincident(g0,g1)
    c: Coincident(g1,g2)
    c: Coincident(g2,g3)
    c: Coincident(g3,g0)
    c: PointOnObject(g0,g-3)
    c: Tangent(g-3,g1)
    c: DistanceY(g1,g1) = 20
    c: Parallel(g3,g1)
    c: Perpendicular(g1,g2)
    c: Parallel(g0,g2)
    c: PointOnObject(g2,g-3)
    c: Angle(g2) = 2.96706
FEATURE [PartDesign::Pocket] Pocket017  label="Pocket - USB flattening"
  BaseFeature = -> Hole007
  Direction = (0,0,-1)
  Length = 30
  Length2 = 5
  Placement = pos=(-25.5,-25.3229,21.8) rot=(0,0,1;0rad)
  Profile = -> Sketch033
  ReferenceAxis = -> Sketch033 [N_Axis]
  Refine = true
  Type = 0
FEATURE [Sketcher::SketchObject] Sketch034
  ExternalGeometry = -> [Pocket017]
  FullyConstrained = true
  MapMode = 5
  Placement = pos=(46.462,-38.0118,21.8) rot=(0.6444,0.540716,0.540716;1.99673rad)
  Support = -> [Pocket017]
  sketch-geometry (11):
    g0: ArcOfCircle CenterX=26.651 CenterY=-5.05 CenterZ=0 NormalX=0 NormalY=0 NormalZ=1 AngleXU=0 Radius=0.5 StartAngle=1.5708 EndAngle=3.14159
    g1: LineSegment StartX=26.651 StartY=-4.55 StartZ=0 EndX=39.001 EndY=-4.55 EndZ=0
    g2: ArcOfCircle CenterX=39.001 CenterY=-5.05 CenterZ=0 NormalX=0 NormalY=0 NormalZ=1 AngleXU=0 Radius=0.5 StartAngle=9.1e-15 EndAngle=1.5708
    g3: LineSegment StartX=39.501 StartY=-5.05 StartZ=0 EndX=39.501 EndY=-18.55 EndZ=0
    g4: ArcOfCircle CenterX=39.001 CenterY=-18.55 CenterZ=0 NormalX=0 NormalY=0 NormalZ=1 AngleXU=0 Radius=0.5 StartAngle=4.71239 EndAngle=6.28319
    g5: LineSegment StartX=39.001 StartY=-19.05 StartZ=0 EndX=26.651 EndY=-19.05 EndZ=0
    g6: ArcOfCircle CenterX=26.651 CenterY=-18.55 CenterZ=0 NormalX=0 NormalY=0 NormalZ=1 AngleXU=0 Radius=0.5 StartAngle=3.14159 EndAngle=4.71239
    g7: LineSegment StartX=26.151 StartY=-18.55 StartZ=0 EndX=26.151 EndY=-5.05 EndZ=0
    g8: GeomPoint X=26.151 Y=-4.55 Z=0
    g9: GeomPoint X=39.501 Y=-19.05 Z=0
    g10: GeomPoint X=32.826 Y=-11.8 Z=0
  constraints (24):
    c: Tangent(g0,g1) = 1.5708
    c: Tangent(g1,g2) = 1.5708
    c: Tangent(g2,g3) = 1.5708
    c: Tangent(g3,g4) = 1.5708
    c: Tangent(g4,g5) = 1.5708
    c: Tangent(g5,g6) = 1.5708
    c: Tangent(g6,g7) = 1.5708
    c: Tangent(g7,g0) = 1.5708
    c: Horizontal(g1)
    c: Horizontal(g5)
    c: Vertical(g3)
    c: Vertical(g7)
    c: Equal(g0,g2)
    c: Equal(g2,g4)
    c: Equal(g4,g6)
    c: PointOnObject(g8,g1)
    c: PointOnObject(g8,g7)
    c: PointOnObject(g9,g3)
    c: PointOnObject(g9,g5)
    c: Radius(g0) = 0.5
    c: DistanceX(g8,g9) = 13.35
    c: DistanceY(g9,g8) = 14.5
    c: Symmetric(g2,g6,g10)
    c: Symmetric(g-3,g-4,g10)
FEATURE [PartDesign::Pocket] Pocket018  label="Pocket - USB Hole"
  BaseFeature = -> Pocket017
  Direction = (-0.984808,0.173648,1e-16)
  Length = 35
  Length2 = 5
  Placement = pos=(-25.5,-25.3229,21.8) rot=(0,0,1;0rad)
  Profile = -> Sketch034
  ReferenceAxis = -> Sketch034 [N_Axis]
  Refine = true
  Type = 0
FEATURE [Sketcher::SketchObject] Sketch035
  ExternalGeometry = -> [Pocket018,Sketch034]
  FullyConstrained = true
  MapMode = 5
  Placement = pos=(46.462,-38.0118,21.8) rot=(0.6444,0.540716,0.540716;1.99673rad)
  Support = -> [Pocket018]
  sketch-geometry (20):
    g0: ArcOfCircle CenterX=26.651 CenterY=-5.05 CenterZ=0 NormalX=0 NormalY=0 NormalZ=1 AngleXU=0 Radius=3.25 StartAngle=1.5708 EndAngle=3.14159
    g1: LineSegment StartX=26.651 StartY=-1.8 StartZ=0 EndX=39.001 EndY=-1.8 EndZ=0
    g2: ArcOfCircle CenterX=39.001 CenterY=-5.05 CenterZ=0 NormalX=0 NormalY=0 NormalZ=1 AngleXU=0 Radius=3.25 StartAngle=2e-16 EndAngle=1.5708
    g3: LineSegment StartX=42.251 StartY=-5.05 StartZ=0 EndX=42.251 EndY=-18.55 EndZ=0
    g4: ArcOfCircle CenterX=39.001 CenterY=-18.55 CenterZ=0 NormalX=0 NormalY=0 NormalZ=1 AngleXU=0 Radius=3.25 StartAngle=4.71239 EndAngle=6.28319
    g5: LineSegment StartX=39.001 StartY=-21.8 StartZ=0 EndX=26.651 EndY=-21.8 EndZ=0
    g6: ArcOfCircle CenterX=26.651 CenterY=-18.55 CenterZ=0 NormalX=0 NormalY=0 NormalZ=1 AngleXU=0 Radius=3.25 StartAngle=3.14159 EndAngle=4.71239
    g7: LineSegment StartX=23.401 StartY=-18.55 StartZ=0 EndX=23.401 EndY=-5.05 EndZ=0
    g8: GeomPoint X=23.401 Y=-1.8 Z=0
    g9: GeomPoint X=42.251 Y=-21.8 Z=0
    g10: ArcOfCircle CenterX=26.651 CenterY=-5.05 CenterZ=0 NormalX=0 NormalY=0 NormalZ=1 AngleXU=0 Radius=2.25 StartAngle=1.5708 EndAngle=3.14159
    g11: LineSegment StartX=26.651 StartY=-2.8 StartZ=0 EndX=39.001 EndY=-2.8 EndZ=0
    g12: ArcOfCircle CenterX=39.001 CenterY=-5.05 CenterZ=0 NormalX=0 NormalY=0 NormalZ=1 AngleXU=0 Radius=2.25 StartAngle=1e-16 EndAngle=1.5708
    g13: LineSegment StartX=41.251 StartY=-5.05 StartZ=0 EndX=41.251 EndY=-18.55 EndZ=0
    g14: ArcOfCircle CenterX=39.001 CenterY=-18.55 CenterZ=0 NormalX=0 NormalY=0 NormalZ=1 AngleXU=0 Radius=2.25 StartAngle=4.71239 EndAngle=6.28319
    g15: LineSegment StartX=39.001 StartY=-20.8 StartZ=0 EndX=26.651 EndY=-20.8 EndZ=0
    g16: ArcOfCircle CenterX=26.651 CenterY=-18.55 CenterZ=0 NormalX=0 NormalY=0 NormalZ=1 AngleXU=0 Radius=2.25 StartAngle=3.14159 EndAngle=4.71239
    g17: LineSegment StartX=24.401 StartY=-18.55 StartZ=0 EndX=24.401 EndY=-5.05 EndZ=0
    g18: GeomPoint X=24.401 Y=-2.8 Z=0
    g19: GeomPoint X=41.251 Y=-20.8 Z=0
  constraints (44):
    c: Tangent(g0,g1) = 1.5708
    c: Tangent(g1,g2) = 1.5708
    c: Tangent(g2,g3) = 1.5708
    c: Tangent(g3,g4) = 1.5708
    c: Tangent(g4,g5) = 1.5708
    c: Tangent(g5,g6) = 1.5708
    c: Tangent(g6,g7) = 1.5708
    c: Tangent(g7,g0) = 1.5708
    c: Horizontal(g1)
    c: Horizontal(g5)
    c: Vertical(g3)
    c: Vertical(g7)
    c: Equal(g0,g2)
    c: Equal(g2,g4)
    c: Equal(g4,g6)
    c: PointOnObject(g8,g1)
    c: PointOnObject(g8,g7)
    c: PointOnObject(g9,g3)
    c: PointOnObject(g9,g5)
    c: Tangent(g10,g11) = 1.5708
    c: Tangent(g11,g12) = 1.5708
    c: Tangent(g12,g13) = 1.5708
    c: Tangent(g13,g14) = 1.5708
    c: Tangent(g14,g15) = 1.5708
    c: Tangent(g15,g16) = 1.5708
    c: Tangent(g16,g17) = 1.5708
    c: Tangent(g17,g10) = 1.5708
    c: Horizontal(g11)
    c: Horizontal(g15)
    c: Vertical(g13)
    c: Vertical(g17)
    c: Equal(g10,g12)
    c: Equal(g12,g14)
    c: Equal(g14,g16)
    c: PointOnObject(g18,g11)
    c: PointOnObject(g18,g17)
    c: PointOnObject(g19,g13)
    c: PointOnObject(g19,g15)
    c: Coincident(g14,g4)
    c: Coincident(g14,g-5)
    c: Coincident(g10,g0)
    c: Coincident(g10,g-4)
    c: DistanceY(g5,g15) = 1
    c: PointOnObject(g5,g-3)
FEATURE [PartDesign::Pad] Pad009
  BaseFeature = -> Pocket018
  Direction = (0.98,-0.17,0)
  Length = 7
  Length2 = 10
  Placement = pos=(-25.5,-25.3229,21.8) rot=(0,0,1;0rad)
  Profile = -> Sketch035
  ReferenceAxis = -> Sketch035 [N_Axis]
  Refine = true
  Type = 0
  UseCustomVector = true
FEATURE [Sketcher::SketchObject] Sketch036
  ExternalGeometry = -> [Cylinder]
  FullyConstrained = true
  MapMode = 5
  Placement = pos=(0,0,30) rot=(0,0,1;0rad)
  Support = -> [Pad]
  sketch-geometry (4):
    g0: LineSegment StartX=-17.5 StartY=-30 StartZ=0 EndX=17.5 EndY=-30 EndZ=0
    g1: LineSegment StartX=17.5 StartY=-30 StartZ=0 EndX=17.5 EndY=-32 EndZ=0
    g2: LineSegment StartX=17.5 StartY=-32 StartZ=0 EndX=-17.5 EndY=-32 EndZ=0
    g3: LineSegment StartX=-17.5 StartY=-32 StartZ=0 EndX=-17.5 EndY=-30 EndZ=0
  constraints (10):
    c: Coincident(g0,g1)
    c: Coincident(g1,g2)
    c: Coincident(g2,g3)
    c: Coincident(g3,g0)
    c: Horizontal(g2)
    c: Vertical(g1)
    c: Vertical(g3)
    c: Symmetric(g0,g0,g-2)
    c: DistanceY(g1,g1) = 2
    c: Coincident(g0,g-3)
FEATURE [PartDesign::Pocket] Pocket019
  BaseFeature = -> Pad009
  Direction = (0,0,-1)
  Length = 28.6
  Length2 = 5
  Placement = pos=(-25.5,-25.3229,21.8) rot=(0,0,1;0rad)
  Profile = -> Sketch036
  ReferenceAxis = -> Sketch036 [N_Axis]
  Refine = true
  Type = 0
FEATURE [Sketcher::SketchObject] Sketch037
  ExternalGeometry = -> [Pocket019]
  FullyConstrained = true
  MapMode = 5
  Placement = pos=(0,0,30) rot=(0,0,1;0rad)
  Support = -> [Pad]
  sketch-geometry (8):
    g0: LineSegment StartX=32.4988 StartY=28.2217 StartZ=0 EndX=45.0107 EndY=15.2813 EndZ=0
    g1: LineSegment StartX=45.0107 StartY=15.2813 StartZ=0 EndX=34.946 EndY=5.54985 EndZ=0
    g2: LineSegment StartX=34.946 StartY=5.54985 StartZ=0 EndX=22.4341 EndY=18.4902 EndZ=0
    g3: LineSegment StartX=22.4341 StartY=18.4902 StartZ=0 EndX=32.4988 EndY=28.2217 EndZ=0
    g4: LineSegment StartX=42.3266 StartY=12.6861 StartZ=0 EndX=43.349 EndY=10.9672 EndZ=0
    g5: LineSegment StartX=33.6158 StartY=29.8807 StartZ=0 EndX=32.4988 EndY=28.2217 EndZ=0
    g6: GeomPoint X=33.6158 Y=29.8807 Z=0
    g7: LineSegment StartX=45.0107 StartY=15.2813 StartZ=0 EndX=46.4485 EndY=16.6715 EndZ=0
  constraints (23):
    c: Coincident(g0,g1)
    c: Coincident(g1,g2)
    c: Coincident(g2,g3)
    c: Coincident(g3,g0)
    c: Parallel(g0,g2)
    c: Parallel(g3,g1)
    c: Perpendicular(g2,g3)
    c: Distance(g0) = 18
    c: Distance(g3) = 14
    c: Perpendicular(g-4,g4)
    c: Distance(g4) = 2
    c: PointOnObject(g5,g-3)
    c: PointOnObject(g6,g-3)
    c: PointOnObject(g6,g5)
    c: Perpendicular(g-3,g5,g6) = 1.5708
    c: Distance(g5) = 2
    c: Coincident(g5,g0)
    c: PointOnObject(g4,g1)
    c: Coincident(g4,g-4)
    c: Coincident(g7,g0)
    c: PointOnObject(g7,g-3)
    c: Distance(g7) = 2
    c: Parallel(g7,g1)
FEATURE [PartDesign::Pocket] Pocket020
  BaseFeature = -> Pocket019
  Direction = (0,0,-1)
  Length = 12
  Length2 = 5
  Placement = pos=(-25.5,-25.3229,21.8) rot=(0,0,1;0rad)
  Profile = -> Sketch037
  ReferenceAxis = -> Sketch037 [N_Axis]
  Refine = true
  Type = 0
FEATURE [PartDesign::Body] Body  label="Deckel"
  AttacherType = Attacher::AttachEngine3D
  Group = -> [Sketch,Pad,Sketch001,Pocket,Cylinder,DatumPlane,Box,DatumPlane001,Sketch002,Pocket001,Sketch003,Pocket002,Sketch004,Pocket003,Sketch005,Pocket004,Sketch027,Hole,Sketch028,Pocket012,Sketch029,Pocket013,Sketch030,Pocket014,DatumLine004,Sketch009,Pocket015,Sketch031,Hole007,Sketch033,Pocket017,Sketch034,Pocket018,Sketch035,Pad009,Sketch036,Pocket019,Sketch037,Pocket020]
  Origin = -> Origin001
  Tip = -> Pocket020
